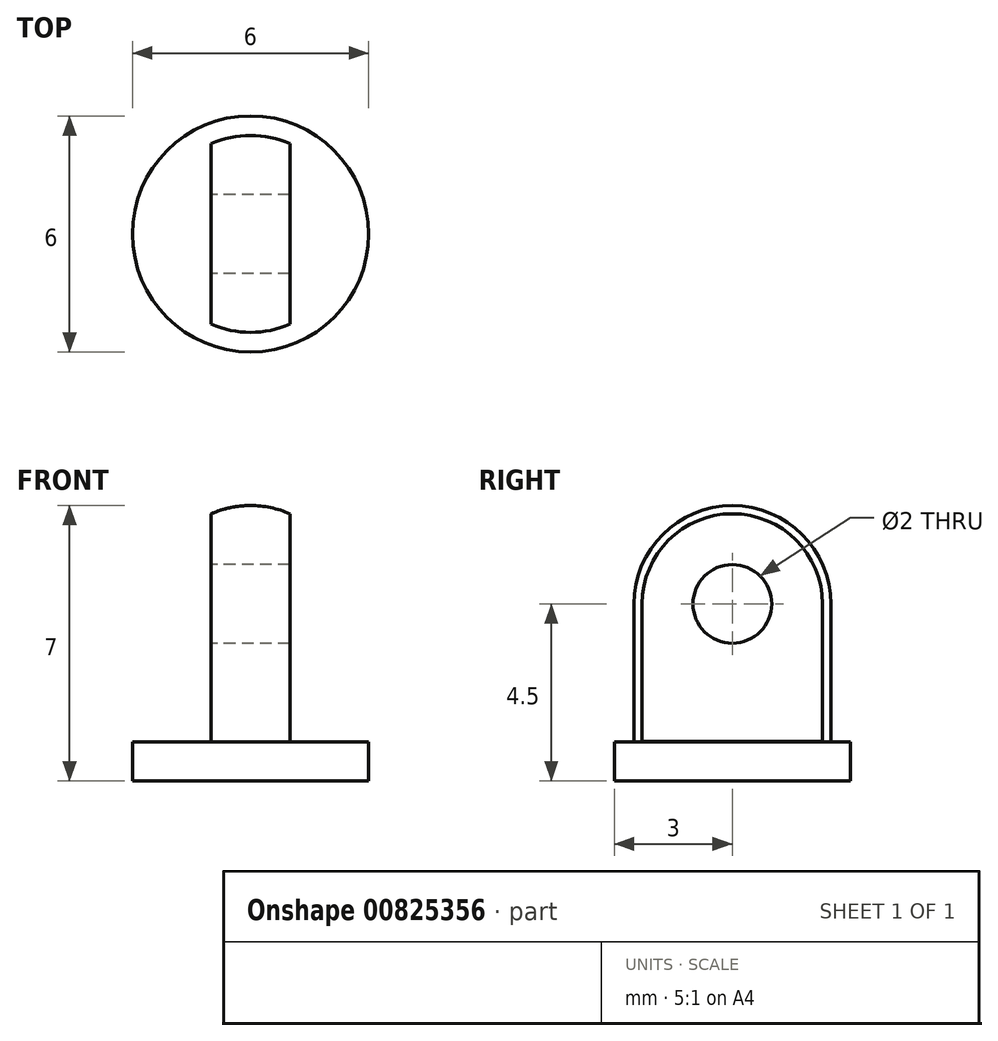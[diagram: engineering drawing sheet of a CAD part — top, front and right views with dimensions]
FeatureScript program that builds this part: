
annotation { "Feature Type Name" : "Feature", "Feature Type Description" : "" }
export const myFeature = defineFeature(function(context is Context, id is Id, definition is map)
    precondition{}
    {
        {
            var Q0;
            Q0=qCreatedBy(makeId("Top.planeOp"),FACE);
            var sketch = newSketch(context, id + "F0", { "sketchPlane" : qUnion([Q0])});
            skCircle(sketch, "E0", {"center": v(0, 0) * mm, "radius": 3 * mm});
            skSolve(sketch);
        }
        {
            var Q0;
            Q0=makeQuery(id+"F0.imprint","IMPRINT",FACE,{"disambiguationData":[TD([[makeQuery(id+"F0.imprint","IMPRINT",EDGE,{"derivedFrom":sQuery(id+"F0.wireOp",EDGE,"E0")}),1.0]])]});
            extrude(context, id + "F1", {"entities" : qUnion([Q0]), "depth" : 1 * mm, "offsetDistance" : 25 * mm});
        }
        {
            var Q0;
            Q0=makeQuery(id+"F1.opExtrude","CAP_FACE",FACE,{"disambiguationData":[OSD([sQuery(id+"F0.wireOp",EDGE,"E0")])],"isStart":false});
            var sketch = newSketch(context, id + "F2", { "sketchPlane" : qUnion([Q0])});
            skCircle(sketch, "E1", {"center": v(0, 0) * mm, "radius": 2.5 * mm});
            skSolve(sketch);
        }
        {
            var Q0;
            Q0=makeQuery(id+"F2.imprint","IMPRINT",FACE,{"disambiguationData":[TD([[makeQuery(id+"F2.imprint","IMPRINT",EDGE,{"derivedFrom":sQuery(id+"F2.wireOp",EDGE,"E1")}),1.0]])]});
            extrude(context, id + "F3", {"entities" : qUnion([Q0]), "operationType" : NewBodyOperationType.ADD, "depth" : 3.5 * mm, "offsetDistance" : 25 * mm});
        }
        {
            var Q0;
            Q0=qCreatedBy(makeId("Front.planeOp"),FACE);
            var sketch = newSketch(context, id + "F4", { "sketchPlane" : qUnion([Q0])});
            skLineSegment(sketch, "E2.bottom", {"start": v(-1, 1) * mm, "end": v(-3, 1) * mm});
            skLineSegment(sketch, "E2.top", {"start": v(-1, 11) * mm, "end": v(-3, 11) * mm});
            skLineSegment(sketch, "E2.left", {"start": v(-1, 1) * mm, "end": v(-1, 11) * mm});
            skLineSegment(sketch, "E2.right", {"start": v(-3, 1) * mm, "end": v(-3, 11) * mm});
            skLineSegment(sketch, "E3.MirrorCS", {"start": v(3, 1) * mm, "end": v(3, 11) * mm});
            skLineSegment(sketch, "E4.MirrorCS", {"start": v(1, 1) * mm, "end": v(1, 11) * mm});
            skLineSegment(sketch, "E5.MirrorCS", {"start": v(1, 11) * mm, "end": v(3, 11) * mm});
            skLineSegment(sketch, "E6.MirrorCS", {"start": v(1, 1) * mm, "end": v(3, 1) * mm});
            skSolve(sketch);
        }
        {
            var Q0;
            Q0=qCreatedBy(makeId("Front.planeOp"),FACE);
            var sketch = newSketch(context, id + "F5", { "sketchPlane" : qUnion([Q0])});
            skArc(sketch, "E7", {"start": v(0, 7) * mm, "mid": v(-1.77, 6.27) * mm, "end": v(-2.5, 4.5) * mm});
            skLineSegment(sketch, "E8", {"start": v(0, 7) * mm, "end": v(0, 4.5) * mm});
            skLineSegment(sketch, "E9", {"start": v(0, 4.5) * mm, "end": v(-2.5, 4.5) * mm});
            skSolve(sketch);
        }
        {
            var Q0;
            Q0=makeQuery(id+"F5.imprint","IMPRINT",FACE,{"disambiguationData":[TD([[makeQuery(id+"F5.imprint","IMPRINT",EDGE,{"derivedFrom":sQuery(id+"F5.wireOp",EDGE,"E7")}),1.0]])]});
            var Q1;
            Q1=sQuery(id+"F5.wireOp",EDGE,"E8");
            revolve(context, id + "F6", {"operationType" : NewBodyOperationType.ADD, "surfaceOperationType" : NewSurfaceOperationType.NEW, "entities" : qUnion([Q0]), "axis" : qUnion([Q1]), "revolveType" : RevolveType.FULL});
        }
        {
            var Q0;
            Q0=makeQuery(id+"F4.imprint","IMPRINT",FACE,{"disambiguationData":[TD([[makeQuery(id+"F4.imprint","IMPRINT",EDGE,{"derivedFrom":sQuery(id+"F4.wireOp",EDGE,"E3.MirrorCS")}),1.0]])]});
            var Q1;
            Q1=makeQuery(id+"F4.imprint","IMPRINT",FACE,{"disambiguationData":[TD([[makeQuery(id+"F4.imprint","IMPRINT",EDGE,{"derivedFrom":sQuery(id+"F4.wireOp",EDGE,"E2.bottom")}),-1.0]])]});
            extrude(context, id + "F7", {"entities" : qUnion([Q0, Q1]), "operationType" : NewBodyOperationType.REMOVE, "endBound" : BoundingType.SYMMETRIC, "oppositeDirection" : true, "depth" : 10 * mm, "offsetDistance" : 25 * mm});
        }
        {
            var Q0;
            Q0=makeQuery(id+"F7.boolean.opBoolean","COPY",FACE,{"derivedFrom":makeQuery(id+"F7.opExtrude","SWEPT_FACE",FACE,{"disambiguationData":[OSD([sQuery(id+"F4.wireOp",EDGE,"E2.left")])]})});
            var sketch = newSketch(context, id + "F8", { "sketchPlane" : qUnion([Q0])});
            skCircle(sketch, "E10", {"center": v(0, 4.5) * mm, "radius": 1 * mm});
            skSolve(sketch);
        }
        {
            var Q0;
            Q0=makeQuery(id+"F8.imprint","IMPRINT",FACE,{"disambiguationData":[TD([[makeQuery(id+"F8.imprint","IMPRINT",EDGE,{"derivedFrom":sQuery(id+"F8.wireOp",EDGE,"E10")}),1.0]])]});
            extrude(context, id + "F9", {"entities" : qUnion([Q0]), "operationType" : NewBodyOperationType.REMOVE, "endBound" : BoundingType.THROUGH_ALL, "oppositeDirection" : true, "depth" : 25 * mm, "offsetDistance" : 25 * mm});
        }
    });
